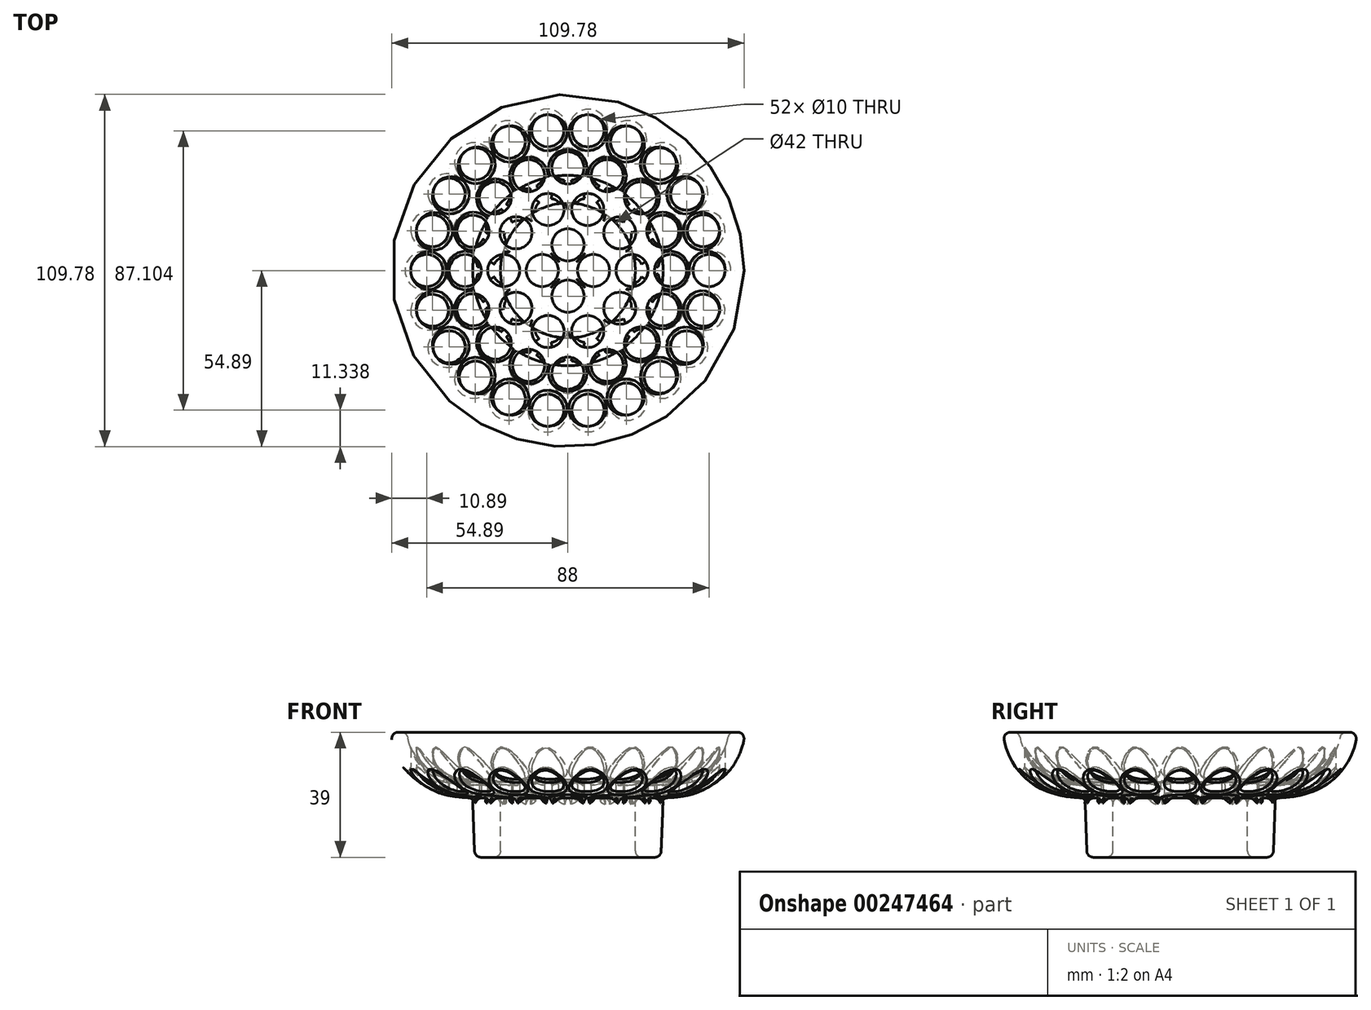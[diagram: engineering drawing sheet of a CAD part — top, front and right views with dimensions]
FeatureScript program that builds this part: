
annotation { "Feature Type Name" : "Feature", "Feature Type Description" : "" }
export const myFeature = defineFeature(function(context is Context, id is Id, definition is map)
    precondition{}
    {
        {
            var Q0;
            Q0=qCreatedBy(makeId("Front.planeOp"),FACE);
            var sketch = newSketch(context, id + "F0", { "sketchPlane" : qUnion([Q0])});
            skLineSegment(sketch, "E0", {"start": v(-23, 0) * mm, "end": v(-27.07, 0) * mm});
            skLineSegment(sketch, "E1", {"start": v(-29.07, 1.92) * mm, "end": v(-29.63, 16.62) * mm});
            skFitSpline(sketch, "E2", {"points": [v(-29.7, 18.5) * mm, v(-54.72, 35.89) * mm, v(-55, 39) * mm], "startDerivative": vector(-74.15, 0) * mm, "endDerivative": vector(0, 6.7) * mm});
            skFitSpline(sketch, "E3.0", {"points": [v(-29.7, 23.5) * mm, v(-32.43, 23.5) * mm, v(-37.07, 24.09) * mm, v(-41.99, 26.08) * mm, v(-45.41, 28.7) * mm, v(-47.75, 31.65) * mm, v(-48.95, 34.1) * mm, v(-49.55, 35.8) * mm, v(-49.78, 36.7) * mm, v(-49.9, 37.26) * mm, v(-49.97, 37.72) * mm, v(-50, 38.13) * mm, v(-50, 38.4) * mm, v(-50, 38.68) * mm, v(-50, 38.88) * mm, v(-50, 39) * mm]});
            skLineSegment(sketch, "E4", {"start": v(-52.89, 39) * mm, "end": v(-51.88, 39) * mm});
            skLineSegment(sketch, "E5", {"start": v(-29.7, 23.5) * mm, "end": v(0, 23.5) * mm});
            skLineSegment(sketch, "E6", {"start": v(0, 23.5) * mm, "end": v(0, 17.86) * mm});
            skLineSegment(sketch, "E7", {"start": v(0, 57.97) * mm, "end": v(0, -37.79) * mm, "construction": true});
            skLineSegment(sketch, "E8", {"start": v(-21, 2) * mm, "end": v(-21, 16.5) * mm});
            skLineSegment(sketch, "E9", {"start": v(-19, 18.5) * mm, "end": v(0, 18.5) * mm});
            skPoint(sketch, "E10.visualSharp", {"position": v(-21, 18.5) * mm});
            skArc(sketch, "E10.filletArc", {"start": v(-19, 18.5) * mm, "mid": v(-20.41, 17.91) * mm, "end": v(-21, 16.5) * mm});
            skPoint(sketch, "E11.visualSharp", {"position": v(-21, 0) * mm});
            skArc(sketch, "E11.filletArc", {"start": v(-23, 0) * mm, "mid": v(-21.59, 0.59) * mm, "end": v(-21, 2) * mm});
            skPoint(sketch, "E12.visualSharp", {"position": v(-29, 0) * mm});
            skArc(sketch, "E12.filletArc", {"start": v(-29.07, 1.92) * mm, "mid": v(-28.46, 0.56) * mm, "end": v(-27.07, 0) * mm});
            skArc(sketch, "E13.filletArc", {"start": v(-29.63, 16.62) * mm, "mid": v(-30.2, 17.95) * mm, "end": v(-31.54, 18.54) * mm});
            skArc(sketch, "E14.filletArc", {"start": v(-52.89, 39) * mm, "mid": v(-54.4, 38.3) * mm, "end": v(-54.87, 36.7) * mm});
            skPoint(sketch, "E15.visualSharp", {"position": v(-50, 39) * mm});
            skArc(sketch, "E15.filletArc", {"start": v(-49.9, 37.34) * mm, "mid": v(-50.59, 38.53) * mm, "end": v(-51.88, 39) * mm});
            skSolve(sketch);
        }
        {
            var Q0;
            Q0=makeQuery(id+"F0.imprint","IMPRINT",FACE,{"disambiguationData":[TD([[makeQuery(id+"F0.imprint","IMPRINT",EDGE,{"derivedFrom":sQuery(id+"F0.wireOp",EDGE,"E0")}),-1.0]])]});
            var Q1;
            Q1=sQuery(id+"F0.wireOp",EDGE,"E7");
            revolve(context, id + "F1", {"entities" : qUnion([Q0]), "axis" : qUnion([Q1]), "revolveType" : RevolveType.FULL});
        }
        {
            var Q0;
            Q0=qCreatedBy(makeId("Top.planeOp"),FACE);
            var sketch = newSketch(context, id + "F2", { "sketchPlane" : qUnion([Q0])});
            skCircle(sketch, "E16", {"center": v(-8, 0) * mm, "radius": 5 * mm});
            skCircle(sketch, "E17.1.0.0", {"center": v(-20, 0) * mm, "radius": 5 * mm});
            skCircle(sketch, "E17.2.0.0", {"center": v(-32, 0) * mm, "radius": 5 * mm});
            skCircle(sketch, "E17.3.0.0", {"center": v(-44, 0) * mm, "radius": 5 * mm});
            skLineSegment(sketch, "E17.direction1", {"start": v(-8, 0) * mm, "end": v(-20, 0) * mm, "construction": true});
            skCircle(sketch, "E18.1.0", {"center": v(-42.22, -12.4) * mm, "radius": 5 * mm});
            skCircle(sketch, "E18.2.0", {"center": v(-37.02, -23.79) * mm, "radius": 5 * mm});
            skCircle(sketch, "E18.3.0", {"center": v(-28.81, -33.25) * mm, "radius": 5 * mm});
            skCircle(sketch, "E18.4.0", {"center": v(-18.28, -40.02) * mm, "radius": 5 * mm});
            skCircle(sketch, "E18.5.0", {"center": v(-6.26, -43.55) * mm, "radius": 5 * mm});
            skCircle(sketch, "E18.6.0", {"center": v(6.26, -43.55) * mm, "radius": 5 * mm});
            skCircle(sketch, "E18.7.0", {"center": v(18.28, -40.02) * mm, "radius": 5 * mm});
            skCircle(sketch, "E18.8.0", {"center": v(28.81, -33.25) * mm, "radius": 5 * mm});
            skCircle(sketch, "E18.9.0", {"center": v(37.02, -23.79) * mm, "radius": 5 * mm});
            skCircle(sketch, "E18.10.0", {"center": v(42.22, -12.4) * mm, "radius": 5 * mm});
            skCircle(sketch, "E18.11.0", {"center": v(44, 0) * mm, "radius": 5 * mm});
            skCircle(sketch, "E18.12.0", {"center": v(42.22, 12.4) * mm, "radius": 5 * mm});
            skCircle(sketch, "E18.13.0", {"center": v(37.02, 23.79) * mm, "radius": 5 * mm});
            skCircle(sketch, "E18.14.0", {"center": v(28.81, 33.25) * mm, "radius": 5 * mm});
            skCircle(sketch, "E18.15.0", {"center": v(18.28, 40.02) * mm, "radius": 5 * mm});
            skCircle(sketch, "E18.16.0", {"center": v(6.26, 43.55) * mm, "radius": 5 * mm});
            skCircle(sketch, "E18.17.0", {"center": v(-6.26, 43.55) * mm, "radius": 5 * mm});
            skCircle(sketch, "E18.18.0", {"center": v(-18.28, 40.02) * mm, "radius": 5 * mm});
            skCircle(sketch, "E18.19.0", {"center": v(-28.81, 33.25) * mm, "radius": 5 * mm});
            skCircle(sketch, "E18.20.0", {"center": v(-37.02, 23.79) * mm, "radius": 5 * mm});
            skCircle(sketch, "E18.21.0", {"center": v(-42.22, 12.4) * mm, "radius": 5 * mm});
            skPoint(sketch, "E18.center", {"position": v(0, 0) * mm});
            skCircle(sketch, "E19.1.0", {"center": v(-29.56, -12.25) * mm, "radius": 5 * mm});
            skCircle(sketch, "E19.2.0", {"center": v(-22.63, -22.63) * mm, "radius": 5 * mm});
            skCircle(sketch, "E19.3.0", {"center": v(-12.25, -29.56) * mm, "radius": 5 * mm});
            skCircle(sketch, "E19.4.0", {"center": v(0, -32) * mm, "radius": 5 * mm});
            skCircle(sketch, "E19.5.0", {"center": v(12.25, -29.56) * mm, "radius": 5 * mm});
            skCircle(sketch, "E19.6.0", {"center": v(22.63, -22.63) * mm, "radius": 5 * mm});
            skCircle(sketch, "E19.7.0", {"center": v(29.56, -12.25) * mm, "radius": 5 * mm});
            skCircle(sketch, "E19.8.0", {"center": v(32, 0) * mm, "radius": 5 * mm});
            skCircle(sketch, "E19.9.0", {"center": v(29.56, 12.25) * mm, "radius": 5 * mm});
            skCircle(sketch, "E19.10.0", {"center": v(22.63, 22.63) * mm, "radius": 5 * mm});
            skCircle(sketch, "E19.11.0", {"center": v(12.25, 29.56) * mm, "radius": 5 * mm});
            skCircle(sketch, "E19.12.0", {"center": v(0, 32) * mm, "radius": 5 * mm});
            skCircle(sketch, "E19.13.0", {"center": v(-12.25, 29.56) * mm, "radius": 5 * mm});
            skCircle(sketch, "E19.14.0", {"center": v(-22.63, 22.63) * mm, "radius": 5 * mm});
            skCircle(sketch, "E19.15.0", {"center": v(-29.56, 12.25) * mm, "radius": 5 * mm});
            skCircle(sketch, "E20.1.0", {"center": v(-16.18, -11.76) * mm, "radius": 5 * mm});
            skCircle(sketch, "E20.2.0", {"center": v(-6.18, -19.02) * mm, "radius": 5 * mm});
            skCircle(sketch, "E20.3.0", {"center": v(6.18, -19.02) * mm, "radius": 5 * mm});
            skCircle(sketch, "E20.4.0", {"center": v(16.18, -11.76) * mm, "radius": 5 * mm});
            skCircle(sketch, "E20.5.0", {"center": v(20, 0) * mm, "radius": 5 * mm});
            skCircle(sketch, "E20.6.0", {"center": v(16.18, 11.76) * mm, "radius": 5 * mm});
            skCircle(sketch, "E20.7.0", {"center": v(6.18, 19.02) * mm, "radius": 5 * mm});
            skCircle(sketch, "E20.8.0", {"center": v(-6.18, 19.02) * mm, "radius": 5 * mm});
            skCircle(sketch, "E20.9.0", {"center": v(-16.18, 11.76) * mm, "radius": 5 * mm});
            skCircle(sketch, "E21.1.0", {"center": v(0, -8) * mm, "radius": 5 * mm});
            skCircle(sketch, "E21.2.0", {"center": v(8, 0) * mm, "radius": 5 * mm});
            skCircle(sketch, "E21.3.0", {"center": v(0, 8) * mm, "radius": 5 * mm});
            skSolve(sketch);
        }
        {
            var Q0;
            Q0 = qSketchRegion(id + "F2", true);
            extrude(context, id + "F3", {"entities" : qUnion([Q0]), "operationType" : NewBodyOperationType.REMOVE, "depth" : 40 * mm, "hasSecondDirection" : true, "secondDirectionOppositeDirection" : false, "secondDirectionDepth" : 18.5 * mm});
        }
        {
            var Q0;
            Q0=makeQuery(id+"F1.opRevolve","SWEPT_FACE",FACE,{"disambiguationData":[OSD([sQuery(id+"F0.wireOp",EDGE,"E3.0")])]});
            var Q1;
            Q1=makeQuery(id+"F1.opRevolve","SWEPT_FACE",FACE,{"disambiguationData":[OSD([sQuery(id+"F0.wireOp",EDGE,"E5")])]});
            var Q2;
            Q2=makeQuery(id+"F1.opRevolve","SWEPT_FACE",FACE,{"disambiguationData":[OSD([sQuery(id+"F0.wireOp",EDGE,"E9")])]});
            var Q3;
            Q3=makeQuery(id+"F1.opRevolve","SWEPT_FACE",FACE,{"disambiguationData":[OSD([sQuery(id+"F0.wireOp",EDGE,"E2")])]});
            fillet(context, id + "F4", {"entities" : qUnion([Q0, Q1, Q2, Q3]), "radius" : 1 * mm, "tangentPropagation" : true, "allowEdgeOverflow" : false});
        }
        {
            var Q0;
            Q0=makeQuery(id+"F1.opRevolve","SWEPT_FACE",FACE,{"disambiguationData":[OSD([sQuery(id+"F0.wireOp",EDGE,"E13.filletArc")])]});
            fillet(context, id + "F5", {"entities" : qUnion([Q0]), "radius" : 1.5 * mm, "tangentPropagation" : true, "allowEdgeOverflow" : false});
        }
        {
            var Q0;
            Q0=makeQuery(id+"F1.opRevolve","SWEPT_FACE",FACE,{"disambiguationData":[OSD([sQuery(id+"F0.wireOp",EDGE,"E10.filletArc")])]});
            fillet(context, id + "F6", {"entities" : qUnion([Q0]), "radius" : 2 * mm, "tangentPropagation" : true, "allowEdgeOverflow" : false});
        }
        {
            var Q0;
            Q0=makeQuery(id+"F3.boolean.opBoolean","COPY",EDGE,{"derivedFrom":makeQuery(id+"F3.opExtrude","CAP_EDGE",EDGE,{"disambiguationData":[OSD([sQuery(id+"F2.wireOp",EDGE,"E19.3.0")])],"isStart":true})});
            var Q1;
            Q1=makeQuery(id+"F3.boolean.opBoolean","COPY",EDGE,{"derivedFrom":makeQuery(id+"F3.opExtrude","CAP_EDGE",EDGE,{"disambiguationData":[OSD([sQuery(id+"F2.wireOp",EDGE,"E19.4.0")])],"isStart":true})});
            var Q2;
            Q2=makeQuery(id+"F3.boolean.opBoolean","COPY",EDGE,{"derivedFrom":makeQuery(id+"F3.opExtrude","CAP_EDGE",EDGE,{"disambiguationData":[OSD([sQuery(id+"F2.wireOp",EDGE,"E19.5.0")])],"isStart":true})});
            var Q3;
            Q3=makeQuery(id+"F3.boolean.opBoolean","COPY",EDGE,{"derivedFrom":makeQuery(id+"F3.opExtrude","CAP_EDGE",EDGE,{"disambiguationData":[OSD([sQuery(id+"F2.wireOp",EDGE,"E19.6.0")])],"isStart":true})});
            var Q4;
            Q4=makeQuery(id+"F3.boolean.opBoolean","COPY",EDGE,{"derivedFrom":makeQuery(id+"F3.opExtrude","CAP_EDGE",EDGE,{"disambiguationData":[OSD([sQuery(id+"F2.wireOp",EDGE,"E19.7.0")])],"isStart":true})});
            var Q5;
            Q5=makeQuery(id+"F3.boolean.opBoolean","COPY",EDGE,{"derivedFrom":makeQuery(id+"F3.opExtrude","CAP_EDGE",EDGE,{"disambiguationData":[OSD([sQuery(id+"F2.wireOp",EDGE,"E19.8.0")])],"isStart":true})});
            var Q6;
            Q6=makeQuery(id+"F3.boolean.opBoolean","COPY",EDGE,{"derivedFrom":makeQuery(id+"F3.opExtrude","CAP_EDGE",EDGE,{"disambiguationData":[OSD([sQuery(id+"F2.wireOp",EDGE,"E19.9.0")])],"isStart":true})});
            var Q7;
            Q7=makeQuery(id+"F3.boolean.opBoolean","COPY",EDGE,{"derivedFrom":makeQuery(id+"F3.opExtrude","CAP_EDGE",EDGE,{"disambiguationData":[OSD([sQuery(id+"F2.wireOp",EDGE,"E19.10.0")])],"isStart":true})});
            var Q8;
            Q8=makeQuery(id+"F3.boolean.opBoolean","COPY",EDGE,{"derivedFrom":makeQuery(id+"F3.opExtrude","CAP_EDGE",EDGE,{"disambiguationData":[OSD([sQuery(id+"F2.wireOp",EDGE,"E19.11.0")])],"isStart":true})});
            var Q9;
            Q9=makeQuery(id+"F3.boolean.opBoolean","COPY",EDGE,{"derivedFrom":makeQuery(id+"F3.opExtrude","CAP_EDGE",EDGE,{"disambiguationData":[OSD([sQuery(id+"F2.wireOp",EDGE,"E19.12.0")])],"isStart":true})});
            var Q10;
            Q10=makeQuery(id+"F3.boolean.opBoolean","COPY",EDGE,{"derivedFrom":makeQuery(id+"F3.opExtrude","CAP_EDGE",EDGE,{"disambiguationData":[OSD([sQuery(id+"F2.wireOp",EDGE,"E19.13.0")])],"isStart":true})});
            var Q11;
            Q11=makeQuery(id+"F3.boolean.opBoolean","COPY",EDGE,{"derivedFrom":makeQuery(id+"F3.opExtrude","CAP_EDGE",EDGE,{"disambiguationData":[OSD([sQuery(id+"F2.wireOp",EDGE,"E19.14.0")])],"isStart":true})});
            var Q12;
            Q12=makeQuery(id+"F3.boolean.opBoolean","COPY",EDGE,{"derivedFrom":makeQuery(id+"F3.opExtrude","CAP_EDGE",EDGE,{"disambiguationData":[OSD([sQuery(id+"F2.wireOp",EDGE,"E19.15.0")])],"isStart":true})});
            var Q13;
            Q13=makeQuery(id+"F3.boolean.opBoolean","COPY",EDGE,{"derivedFrom":makeQuery(id+"F3.opExtrude","CAP_EDGE",EDGE,{"disambiguationData":[OSD([sQuery(id+"F2.wireOp",EDGE,"E17.2.0.0")])],"isStart":true})});
            var Q14;
            Q14=makeQuery(id+"F3.boolean.opBoolean","COPY",EDGE,{"derivedFrom":makeQuery(id+"F3.opExtrude","CAP_EDGE",EDGE,{"disambiguationData":[OSD([sQuery(id+"F2.wireOp",EDGE,"E19.1.0")])],"isStart":true})});
            var Q15;
            Q15=makeQuery(id+"F3.boolean.opBoolean","COPY",EDGE,{"derivedFrom":makeQuery(id+"F3.opExtrude","CAP_EDGE",EDGE,{"disambiguationData":[OSD([sQuery(id+"F2.wireOp",EDGE,"E19.2.0")])],"isStart":true})});
            fillet(context, id + "F7", {"entities" : qUnion([Q0, Q1, Q2, Q3, Q4, Q5, Q6, Q7, Q8, Q9, Q10, Q11, Q12, Q13, Q14, Q15]), "radius" : 1 * mm, "tangentPropagation" : true, "allowEdgeOverflow" : false});
        }
        {
            var Q0;
            Q0=makeQuery(id+"F3.boolean.opBoolean","COPY",EDGE,{"disambiguationData":[OD(0.0)],"derivedFrom":makeQuery(id+"F3.opExtrude","CAP_EDGE",EDGE,{"disambiguationData":[OSD([sQuery(id+"F2.wireOp",EDGE,"E20.3.0")])],"isStart":true})});
            var Q1;
            Q1=makeQuery(id+"F3.boolean.opBoolean","COPY",EDGE,{"disambiguationData":[OD(0.0)],"derivedFrom":makeQuery(id+"F3.opExtrude","CAP_EDGE",EDGE,{"disambiguationData":[OSD([sQuery(id+"F2.wireOp",EDGE,"E20.4.0")])],"isStart":true})});
            var Q2;
            Q2=makeQuery(id+"F3.boolean.opBoolean","COPY",EDGE,{"disambiguationData":[OD(0.0)],"derivedFrom":makeQuery(id+"F3.opExtrude","CAP_EDGE",EDGE,{"disambiguationData":[OSD([sQuery(id+"F2.wireOp",EDGE,"E20.5.0")])],"isStart":true})});
            var Q3;
            Q3=makeQuery(id+"F3.boolean.opBoolean","COPY",EDGE,{"disambiguationData":[OD(0.0)],"derivedFrom":makeQuery(id+"F3.opExtrude","CAP_EDGE",EDGE,{"disambiguationData":[OSD([sQuery(id+"F2.wireOp",EDGE,"E20.6.0")])],"isStart":true})});
            var Q4;
            Q4=makeQuery(id+"F3.boolean.opBoolean","COPY",EDGE,{"disambiguationData":[OD(0.0)],"derivedFrom":makeQuery(id+"F3.opExtrude","CAP_EDGE",EDGE,{"disambiguationData":[OSD([sQuery(id+"F2.wireOp",EDGE,"E20.7.0")])],"isStart":true})});
            var Q5;
            Q5=makeQuery(id+"F3.boolean.opBoolean","COPY",EDGE,{"disambiguationData":[OD(0.0)],"derivedFrom":makeQuery(id+"F3.opExtrude","CAP_EDGE",EDGE,{"disambiguationData":[OSD([sQuery(id+"F2.wireOp",EDGE,"E20.8.0")])],"isStart":true})});
            var Q6;
            Q6=makeQuery(id+"F3.boolean.opBoolean","COPY",EDGE,{"disambiguationData":[OD(0.0)],"derivedFrom":makeQuery(id+"F3.opExtrude","CAP_EDGE",EDGE,{"disambiguationData":[OSD([sQuery(id+"F2.wireOp",EDGE,"E20.9.0")])],"isStart":true})});
            var Q7;
            Q7=makeQuery(id+"F3.boolean.opBoolean","COPY",EDGE,{"disambiguationData":[OD(0.0)],"derivedFrom":makeQuery(id+"F3.opExtrude","CAP_EDGE",EDGE,{"disambiguationData":[OSD([sQuery(id+"F2.wireOp",EDGE,"E20.1.0")])],"isStart":true})});
            var Q8;
            Q8=makeQuery(id+"F3.boolean.opBoolean","COPY",EDGE,{"disambiguationData":[OD(0.0)],"derivedFrom":makeQuery(id+"F3.opExtrude","CAP_EDGE",EDGE,{"disambiguationData":[OSD([sQuery(id+"F2.wireOp",EDGE,"E20.2.0")])],"isStart":true})});
            var Q9;
            Q9=makeQuery(id+"F3.boolean.opBoolean","COPY",EDGE,{"disambiguationData":[OD(0.0)],"derivedFrom":makeQuery(id+"F3.opExtrude","CAP_EDGE",EDGE,{"disambiguationData":[OSD([sQuery(id+"F2.wireOp",EDGE,"E17.1.0.0")])],"isStart":true})});
            fillet(context, id + "F8", {"entities" : qUnion([Q0, Q1, Q2, Q3, Q4, Q5, Q6, Q7, Q8, Q9]), "radius" : 1.5 * mm, "tangentPropagation" : true, "allowEdgeOverflow" : false});
        }
    });
